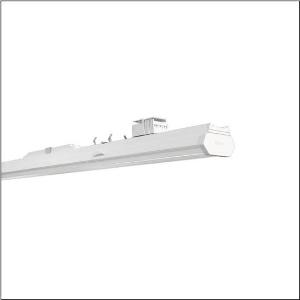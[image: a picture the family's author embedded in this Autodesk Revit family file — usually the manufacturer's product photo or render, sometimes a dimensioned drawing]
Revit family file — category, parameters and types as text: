
# Revit family: licross_r__11_protected_mo_51td127n485g_dbd9
name_source: partatom
category: Lighting Fixtures
units: mm (PartAtom-declared; Revit-internal decimal feet)

## family parameters
Cut with Voids When Loaded = No
Host = Face
Light Source = No
Part Type = Normal
Room Calculation Point = No
Round Connector Dimension = Use Diameter
Shared = No

## types (1)
- Licross® 11 Protected MO (1 x LED, 8720 lm, 48.6 W, 4000K)
    Apparent Load = 49 VA
    CIE Flux Codes = 73 92 98 99 100
    Color Rendering = 80
    Color Temperature = 4000K
    Default Elevation = 1800 mm
    Description = Licross® 11 Protected MO, luminaire insert, of sheet steel, galvanised, coil coated, white, length: 1.500mm, width: 90mm, height: 101mm, LED rated luminous flux: 8.720lm, light colour: 840, control gear: ON/OFF, with plug, 3-pole, with phase selection, mains connection: 220..240V, AC, 50/60Hz, rated input power: 49W, halogen-free wiring, primary light control with lens, of plastic, primary optical cover: cover, of PMMA, light emission: direct distribution, primary light characteristic: symmetric, protection rating (complete): IP54, insulation class (complete): insulation class I (protective earthing), certification: CE, ENEC, VDE, UKCA, protection symbol: D if used in an environment with non-conductive dust loads with corresponding accessories, impact resistance: IK06, permissible ambient temperature for indoor applications: -25..+35°C, corresponds to IFS (International Featured Standards) requirements for safety and quality in the food industry, reducing of maximum allowable ambient temperature of 5°C with ceiling mounting, LABS conformity tested according to VDMA 24364:2018-05, packaging unit: 1 piece
    Height = 92 mm
    Lamp = 1 x LED
    Lamp Light Flux = 8720 lm
    Lamp Power = 48.6 W
    Lamp count = 1
    Length = 1500 mm
    Luminous efficacy = 179 lm/W
    Manufacturer = Siteco
    ModVariant = No
    Model = 51TD127N485G
    Mounting Place = Ceiling
    Mounting Type = Pendant
    Number of Poles = 1
    OnlyDefault = Yes
    Power Factor = 1
    Product Name = Licross® 11 Protected MO
    Product group = luminaire insert
    ProductGroupID = 901
    Protection Class = Protection class I
    Protection Degree = IP 54
    RLX_Detail_Level = 1
    RLX_Emergency_Light_Flux = 0 lm
    RLX_Emergency_Type = 0
    RLX_Emergency_Type_DB = No
    RlxData = <blob elided: 20637 chars, md5=70535b5c>
    Socket = socket
    Standby Power = 0 W
    System Light Flux = 8720 lm
    System Power = 49 W
    Type Comments = Product without accessories
    Type Image = l_1256145.jpg
    URL = http://relux.com
    VarID = ---
    Voltage = 0 V
    Weight = 0.00 kg
    Width = 88 mm

## geometry (parser evidence)
native form markers: Blend x4, Sweep x11
no freeform markers — native parametric forms only
